# Revit family: b1294e88-953c-49a6-8a68-adaf22be3f48
name_source: partatom
category: Mechanical Equipment
revit_build: Autodesk Revit 2016 (Build: 20161004_0715(x64)
units: mm (PartAtom-declared; Revit-internal decimal feet)

## family parameters
Cut with Voids When Loaded = No
Host = Face
OmniClass Number = 23.75.10.24.21.27.21
OmniClass Title = Packaged Terminal Air Conditioning Units
Part Type = Normal
Room Calculation Point = No
Round Connector Dimension = Use Diameter
Shared = No

## types (1)
- (See Type Catalog)
    04 CSI = 23 81 00
    95 CSI = 15730
    Airflow on High = 385 CFM
    Airflow on Low = 295 CFM
    Airflow on Medium = 320 CFM
    Amperage = 3 A
    Assembly Code = D3050
    Compressor LRA = 0 A
    Compressor RLA = 0 A
    Cooling Output = 2256.7 W
    Default Elevation = 4' - 0"
    Dehumidification = 3.2
    Depth = 1' - 9 1/4"
    Description = Packaged Terminal Air Conditioner for smart individuals.
    EER Rating = 12
    Fan Horsepower = 0.0254
    Frequency = 60 Hz
    Height = 1' - 4"
    Load Classification = HVAC
    Number of Poles = 1
    Phase = 1
    Power Consumption for Cooling = 0 W
    Power Factor = 0.97
    R-410A Charge Capacity = 23.63 CF
    Sensible Heat Ratio = 0.84
    Subcategory = Commercial Air Conditioning is very fair.
    Type Image = <None>
    Vent Airflow = 75 CFM
    Voltage = 230 V
    Voltage Range = 253-187 V
    Weight = 108.00 lb
    Width = 3' - 6"
    ecoScorecard Product Page = http://ecoscorecard.com

## geometry (parser evidence)
native form markers: Sweep x2
no freeform markers — native parametric forms only
